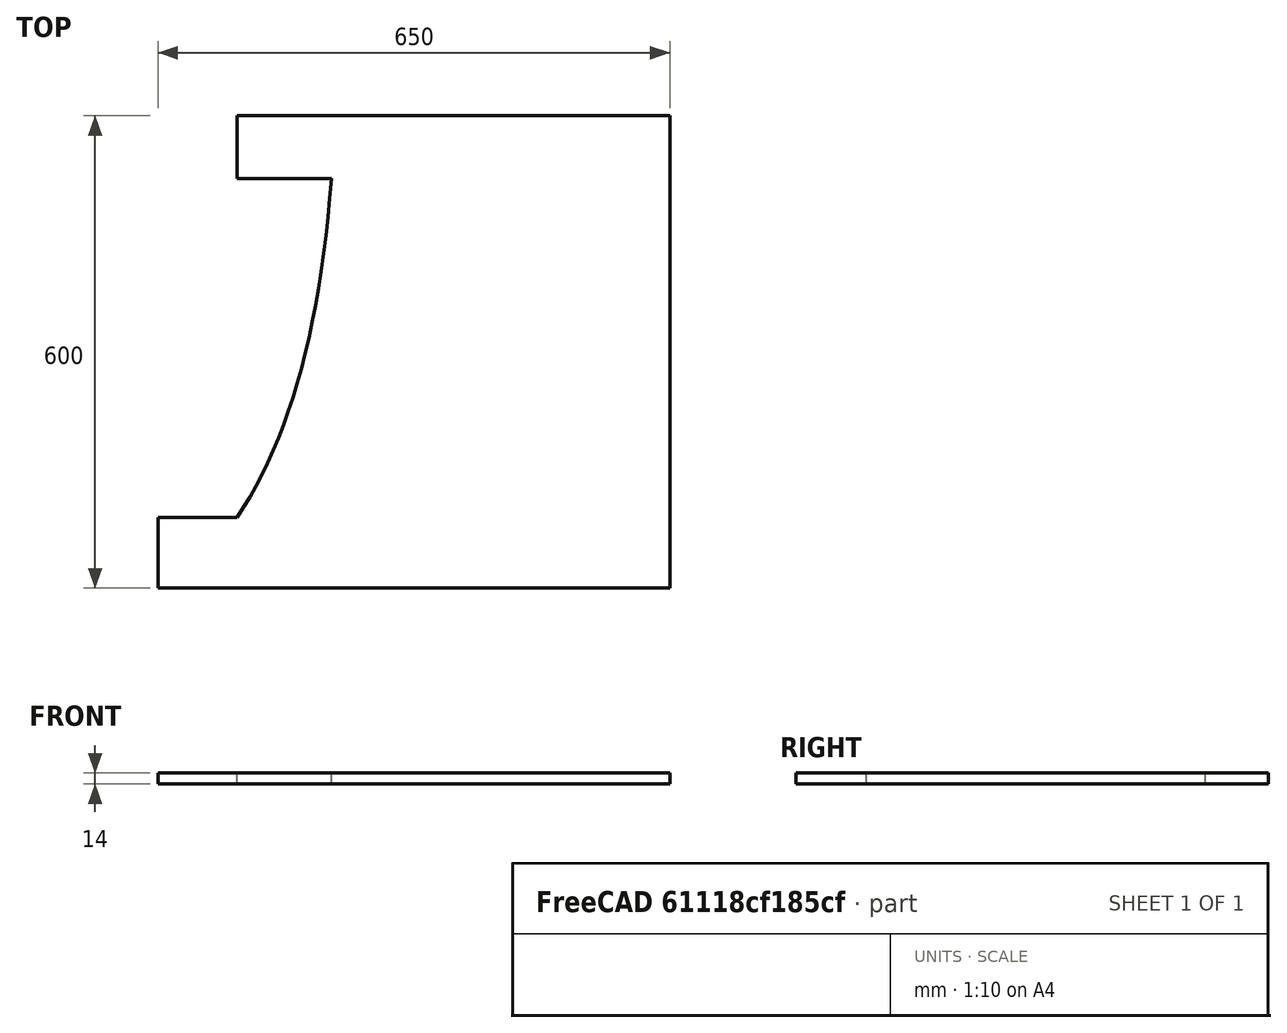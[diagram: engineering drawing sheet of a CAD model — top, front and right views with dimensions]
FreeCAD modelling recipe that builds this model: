
FCSTD DOCUMENT  (FreeCAD 0.18R16131 (Git))
Label: Flange
License: All rights reserved
LicenseURL: http://en.wikipedia.org/wiki/All_rights_reserved
objects: Sketcher::SketchObject×1, PartDesign::Pad×1, PartDesign::Body×1
note: 4 computed .brp shape members not serialized (recipe doc carries the construction recipe); baked Part::Feature solids carry a one-line shape summary decoded from their .brp

FEATURE [Sketcher::SketchObject] Sketch
  MapMode = 5
  Support = -> [XY_Plane]
  sketch-geometry (13):
    g0: LineSegment StartX=0 StartY=0 StartZ=0 EndX=650 EndY=0 EndZ=0
    g1: LineSegment StartX=650 StartY=0 StartZ=0 EndX=650 EndY=600 EndZ=0
    g2: LineSegment StartX=650 StartY=600 StartZ=0 EndX=100 EndY=600 EndZ=0
    g3: LineSegment StartX=100 StartY=600 StartZ=0 EndX=100 EndY=520 EndZ=0
    g4: LineSegment StartX=100 StartY=520 StartZ=0 EndX=220 EndY=520 EndZ=0
    g5: LineSegment StartX=0 StartY=0 StartZ=0 EndX=0 EndY=90 EndZ=0
    g6: LineSegment StartX=0 StartY=90 StartZ=0 EndX=100 EndY=90 EndZ=0
    g7: Circle [constr] CenterX=220 CenterY=520 CenterZ=0 NormalX=0 NormalY=0 NormalZ=1 AngleXU=0 Radius=9
    g8: Circle [constr] CenterX=198.507 CenterY=233.641 CenterZ=0 NormalX=0 NormalY=0 NormalZ=1 AngleXU=0 Radius=9
    g9: Circle [constr] CenterX=100 CenterY=90 CenterZ=0 NormalX=0 NormalY=0 NormalZ=1 AngleXU=0 Radius=9
    g10: BSplineCurve PolesCount=3 KnotsCount=2 Degree=2 IsPeriodic=0
    g11: GeomPoint [constr] X=220 Y=520 Z=0
    g12: GeomPoint [constr] X=100 Y=90 Z=0
  constraints (33):
    c: Coincident(g-1,g0)
    c: PointOnObject(g0,g-1)
    c: Coincident(g0,g1)
    c: Vertical(g1)
    c: Coincident(g1,g2)
    c: Horizontal(g2)
    c: Coincident(g2,g3)
    c: Vertical(g3)
    c: Coincident(g3,g4)
    c: Horizontal(g4)
    c: Coincident(g5,g0)
    c: PointOnObject(g5,g-2)
    c: Coincident(g6,g5)
    c: Coincident(g10,g4)
    c: Radius(g7) = 9
    c: Equal(g7,g8)
    c: Equal(g7,g9)
    c: Coincident(g10,g6)
    c: InternalAlignment(g7,g10)
    c: InternalAlignment(g8,g10)
    c: InternalAlignment(g9,g10)
    c: InternalAlignment(g11,g10)
    c: InternalAlignment(g12,g10)
    c: DistanceY(g1,g1) = 600
    c: DistanceX(g0,g0) = 650
    c: DistanceY(g3,g3) = 80
    c: DistanceY(g5,g5) = 90
    c: Horizontal(g6)
    c: DistanceX(g6,g6) = 100
    c: DistanceX(g4,g4) = 120
    c: DistanceX(g2,g2) = 550
    c: DistanceX(g8) = 198.507
    c: DistanceY(g8) = 233.641
FEATURE [PartDesign::Pad] Pad
  Length = 14
  Length2 = 100
  Profile = -> Sketch
  Type = 0
FEATURE [PartDesign::Body] Body
  Group = -> [Sketch,Pad]
  Origin = -> Origin
  Tip = -> Pad
